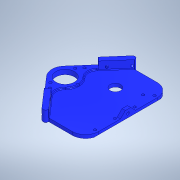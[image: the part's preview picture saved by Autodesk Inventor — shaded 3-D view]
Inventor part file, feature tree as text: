
AUTODESK INVENTOR PART (.ipt)
format: ipt  version: 2022 (Build 260153000, 153)  size: 400,896 bytes
history: native  units: in
note: dims shown in document units (in); Inventor stores cm internally (conversion verified against a paired STEP export)
features: reference x22, sketch x14, extrude x9, other x7, hole x5, projected_geometry x4, fillet x3, mirror x1, chamfer x1
ambient origin geometry x8: Origin, YZ Plane, XZ Plane, XY Plane, X Axis, Y Axis, Z Axis, Center Point
bodies: Solid3 (feature_tree)
feature tree (66):
  extrude  "Extrusion13"  Depth=2.1654in
  extrude  "Extrusion14"  Depth=0.4433in TaperAngle=0.0deg
  mirror  "Mirror4"
  extrude  "Extrusion25"  Depth=0.1969in TaperAngle=0.0deg
  extrude  "Extrusion26"  Depth=0.7874in
  extrude  "Extrusion28"  Depth=0.1969in
  extrude  "Extrusion35"  Depth=0.0787in
  extrude  "Extrusion38"  Depth=1.1024in
  extrude  "Extrusion39"  Depth=0.3937in TaperAngle=0.0deg
  hole  "Hole5"  [1 undecoded]
  fillet  "Fillet3"  Radius=0.4724in
  hole  "Hole6"  [1 undecoded]
  fillet  "Fillet4"  Radius=1.7717in
  chamfer  "Chamfer3"  Distance=0.3937in
  hole  "Hole7"  [1 undecoded]
  hole  "Hole8"  [1 undecoded]
  extrude  "Extrusion40"  Depth=0.0394in TaperAngle=45.0deg
  hole  "Hole9"  [1 undecoded]
  fillet  "Fillet5"  Radius=0.315in
  sketch  "Sketch14"  dims[d94=0.9646in d95=2.1654in]
  sketch  "Sketch15"  dims[d96=1.7717in d97=0.4433in d98=0.0in]
  projected_geometry  "Projected Loop7"
  sketch  "Sketch26"  dims[d99=2.5561in d100=0.1969in d101=0.0in]
  sketch  "Sketch27"  dims[d137=0.7874in d138=1.5748in]
  sketch  "Sketch29"  dims[d139=0.1969in d140=0.0in d141=1.1024in]
  sketch  "Sketch37"  dims[d143=0.0787in d144=0.0in d145=0.5906in]
  projected_geometry  "Projected Loop19"
  sketch  "Sketch40"  dims[d146=1.1024in d149=1.1024in]
  sketch  "Sketch41"  dims[d151=0.6299in d152=0.3937in d153=0.0in]
  projected_geometry  "Projected Loop20"
  sketch  "Sketch42"  dims[d185=0.0in d186=0.0in d198=0.4724in d199=0.4724in]
  sketch  "Sketch43"  dims[d200=0.0in d201=0.0in d202=1.5354in d203=1.7717in]
  reference  "Reference5"
  reference  "Reference6"
  reference  "Reference7"
  reference  "Reference8"
  reference  "Reference9"
  reference  "Reference10"
  reference  "Reference11"
  reference  "Reference12"
  reference  "Reference13"
  reference  "Reference14"
  reference  "Reference15"
  reference  "Reference16"
  reference  "Reference17"
  sketch  "Sketch44"  dims[d204=1.8504in]
  reference  "Reference18"
  reference  "Reference19"
  sketch  "Sketch45"  dims[d205=1.8504in d206=0.3937in d207=0.0in]
  reference  "Reference20"
  reference  "Reference21"
  sketch  "Sketch46"  dims[d208=0.1575in d209=0.2362in d210=0.248in d211=0.0787in d212=90.0deg d213=0.315in d214=0.8108in d215=0.1575in]
  projected_geometry  "Projected Loop21"
  sketch  "Sketch47"  dims[d216=0.1575in d217=0.315in d218=0.1575in d219=0.0787in d220=90.0deg d221=0.2756in d222=0.8108in d223=0.0394in d224=0.0394in d225=0.0787in d226=45.0deg d227=0.1575in d228=0.2362in d229=0.248in d230=0.0787in d231=90.0deg d232=0.315in d233=0.8108in d234=0.1575in d235=0.2362in d236=0.1575in d237=0.0787in d238=90.0deg d239=0.315in d240=0.8108in d241=0.2913in d242=0.315in d243=135.0deg d244=0.1969in d245=0.0in d246=0.1575in d247=0.2362in d248=0.1575in d249=0.0787in d250=90.0deg d251=0.315in d252=0.0in d253=0.7874in d93=0.1575in d107=0.0197in d108=0.0344in d109=0.0197in d110=0.0344in d154=0.0197in d155=0.0344in]
  reference  "Reference22"
  reference  "Reference23"
  reference  "Reference24"
  reference  "Reference25"
  reference  "Reference26"
  parser-record x1  (decoder bookkeeping rows leaked as tree rows — omitted from the tree; the rows remain in map.json)
  other  "Main Body.iam"
  other  "Base Plate:1"
  other  "Front Armor:1"
  other  "Front Armor:2"
  other  "ESC Mount:1"
  other  "ESC Mount:2"
note: 5 required parameter values undecoded (feature->parameter linkage not recoverable at this tier; creation-order binding heuristic only, values carry confidence <= 0.55)
note: 1 file-system path scrubbed to <path> (originals preserved in map.json)
